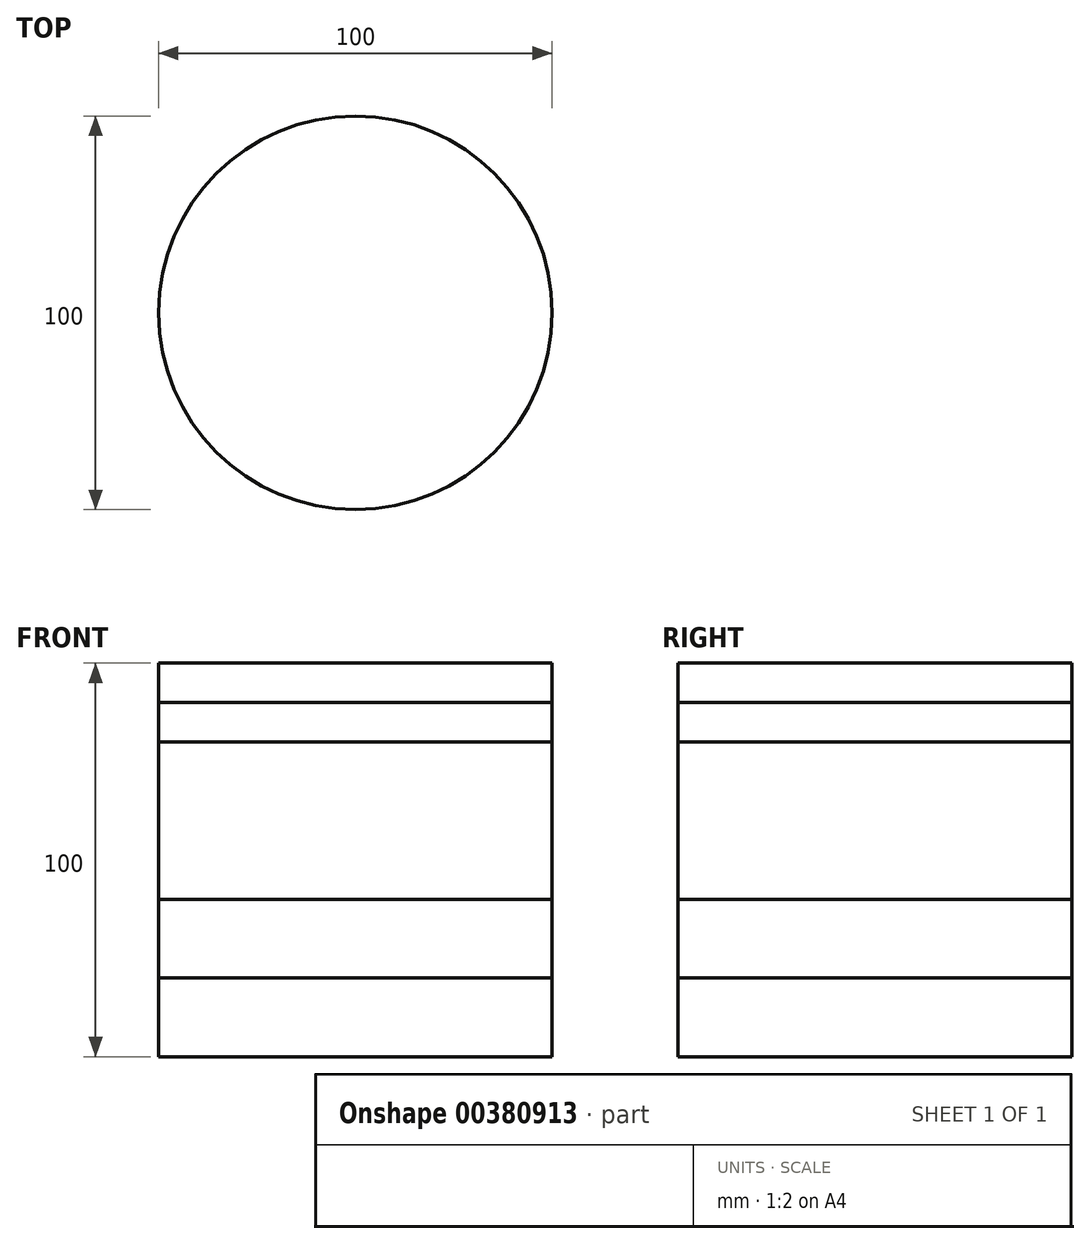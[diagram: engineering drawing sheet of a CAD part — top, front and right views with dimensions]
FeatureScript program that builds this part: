
annotation { "Feature Type Name" : "Feature", "Feature Type Description" : "" }
export const myFeature = defineFeature(function(context is Context, id is Id, definition is map)
    precondition{}
    {
        {
            var Q0;
            Q0=qCreatedBy(makeId("Top.planeOp"),FACE);
            var sketch = newSketch(context, id + "F0", { "sketchPlane" : qUnion([Q0])});
            skCircle(sketch, "E0", {"center": v(0, 0) * mm, "radius": 50 * mm});
            skSolve(sketch);
        }
        {
            var Q0;
            Q0 = qSketchRegion(id + "F0", true);
            extrude(context, id + "F1", {"entities" : qUnion([Q0]), "depth" : 20 * mm});
        }
        {
            var Q0;
            Q0=makeQuery(id+"F1.opExtrude","CAP_FACE",FACE,{"disambiguationData":[OSD([sQuery(id+"F0.wireOp",EDGE,"E0")])],"isStart":false});
            var sketch = newSketch(context, id + "F2", { "sketchPlane" : qUnion([Q0])});
            skCircle(sketch, "E1.0", {"center": v(0, 0) * mm, "radius": 50 * mm});
            skSolve(sketch);
        }
        {
            var Q0;
            Q0 = qSketchRegion(id + "F2", true);
            extrude(context, id + "F3", {"entities" : qUnion([Q0]), "depth" : 20 * mm});
        }
        {
            var Q0;
            Q0 = qSketchRegion(id + "F0", true);
            extrude(context, id + "F4", {"entities" : qUnion([Q0]), "depth" : 100 * mm});
        }
        {
            var Q0;
            Q0=makeQuery(id+"F4.opExtrude","CAP_FACE",FACE,{"disambiguationData":[OSD([sQuery(id+"F0.wireOp",EDGE,"E0")])],"isStart":false});
            extrude(context, id + "F5", {"entities" : qUnion([Q0]), "oppositeDirection" : true, "depth" : 20 * mm});
        }
        {
            var Q0;
            Q0=makeQuery(id+"F5.opExtrude","CAP_FACE",FACE,{"disambiguationData":[OSD([sQuery(id+"F0.wireOp",EDGE,"E0")])],"isStart":true});
            extrude(context, id + "F6", {"entities" : qUnion([Q0]), "oppositeDirection" : true, "depth" : 10 * mm});
        }
        {
            var Q0;
            Q0=makeQuery(id+"F6.opExtrude","CAP_FACE",FACE,{"disambiguationData":[OSD([sQuery(id+"F0.wireOp",EDGE,"E0")])],"isStart":false});
            extrude(context, id + "F7", {"entities" : qUnion([Q0]), "depth" : 10 * mm});
        }
    });
